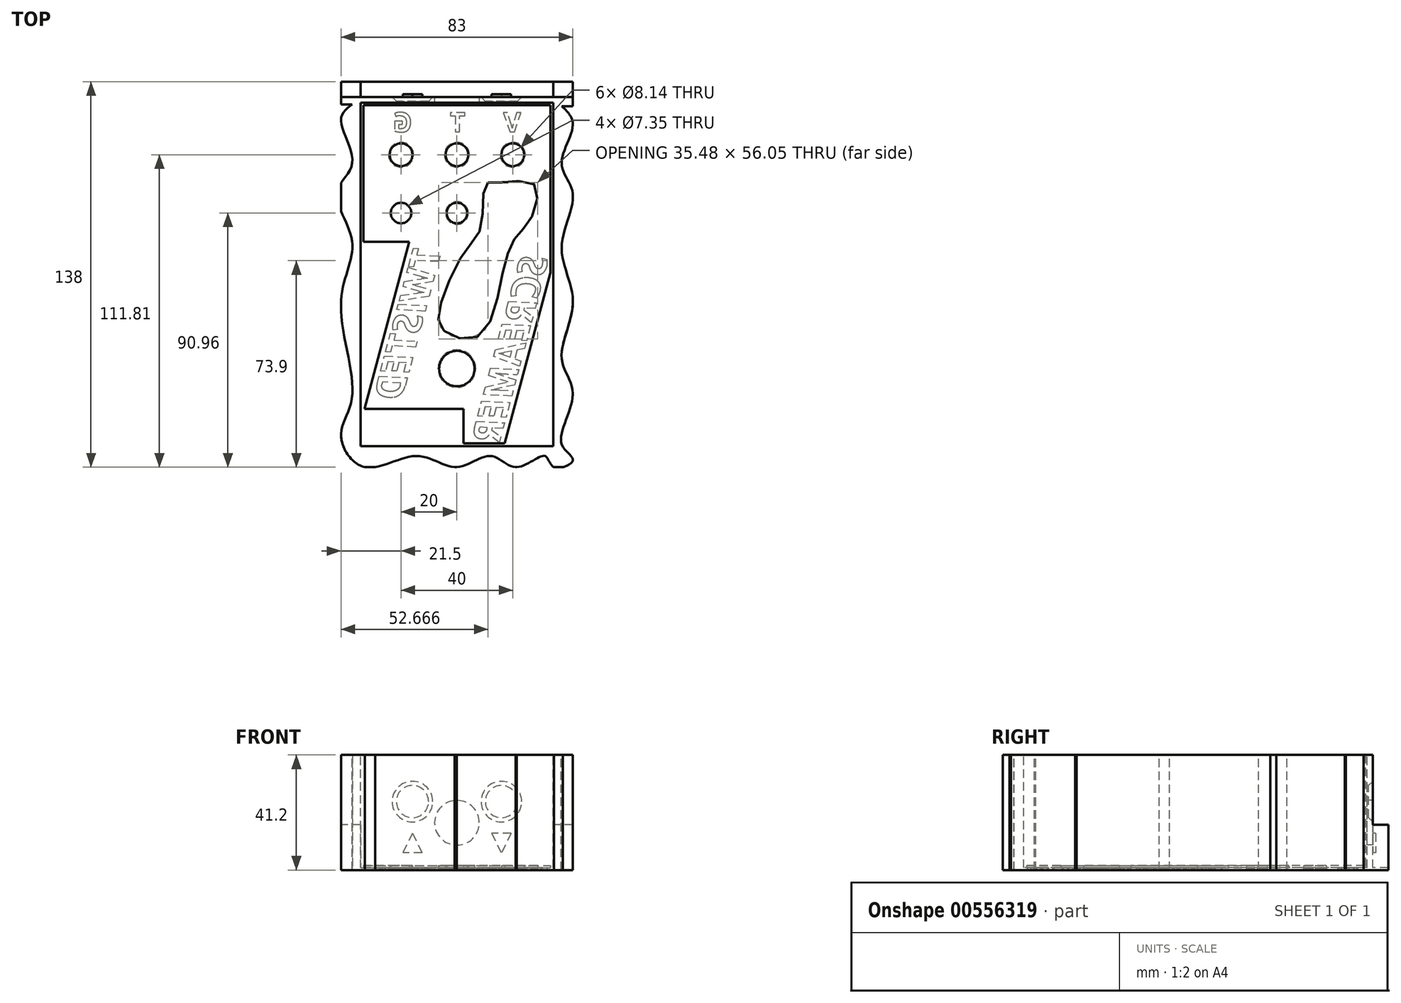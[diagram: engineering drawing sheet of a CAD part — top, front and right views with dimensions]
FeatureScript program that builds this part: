
annotation { "Feature Type Name" : "Feature", "Feature Type Description" : "" }
export const myFeature = defineFeature(function(context is Context, id is Id, definition is map)
    precondition{}
    {
        {
            var Q0;
            Q0=qCreatedBy(makeId("Top.planeOp"),FACE);
            var sketch = newSketch(context, id + "F0", { "sketchPlane" : qUnion([Q0])});
            skLineSegment(sketch, "E0.bottom", {"start": v(-41.5, 69) * mm, "end": v(41.5, 69) * mm});
            skLineSegment(sketch, "E0.top", {"start": v(-41.5, -69) * mm, "end": v(41.5, -69) * mm});
            skLineSegment(sketch, "E0.left", {"start": v(-41.5, 69) * mm, "end": v(-41.5, -69) * mm});
            skLineSegment(sketch, "E0.right", {"start": v(41.5, 69) * mm, "end": v(41.5, -69) * mm});
            skSolve(sketch);
        }
        {
            var Q0;
            Q0=makeQuery(id+"F0.imprint","IMPRINT",FACE,{"disambiguationData":[TD([[makeQuery(id+"F0.imprint","IMPRINT",EDGE,{"derivedFrom":sQuery(id+"F0.wireOp",EDGE,"E0.bottom")}),-1.0]])]});
            extrude(context, id + "F1", {"entities" : qUnion([Q0]), "depth" : 41.2 * mm, "offsetDistance" : 25 * mm});
        }
        {
            var Q0;
            Q0=makeQuery(id+"F1.opExtrude","CAP_FACE",FACE,{"disambiguationData":[OSD([sQuery(id+"F0.wireOp",EDGE,"E0.bottom"),sQuery(id+"F0.wireOp",EDGE,"E0.top"),sQuery(id+"F0.wireOp",EDGE,"E0.left"),sQuery(id+"F0.wireOp",EDGE,"E0.right")])],"isStart":false});
            var sketch = newSketch(context, id + "F2", { "sketchPlane" : qUnion([Q0])});
            skLineSegment(sketch, "E1.bottom", {"start": v(-34.5, 61.5) * mm, "end": v(34.5, 61.5) * mm});
            skLineSegment(sketch, "E1.top", {"start": v(-34.5, -61.5) * mm, "end": v(34.5, -61.5) * mm});
            skLineSegment(sketch, "E1.left", {"start": v(-34.5, 61.5) * mm, "end": v(-34.5, -61.5) * mm});
            skLineSegment(sketch, "E1.right", {"start": v(34.5, 61.5) * mm, "end": v(34.5, -61.5) * mm});
            skSolve(sketch);
        }
        {
            var Q0;
            Q0=makeQuery(id+"F2.imprint","IMPRINT",FACE,{"disambiguationData":[TD([[makeQuery(id+"F2.imprint","IMPRINT",EDGE,{"derivedFrom":sQuery(id+"F2.wireOp",EDGE,"E1.bottom")}),-1.0]])]});
            extrude(context, id + "F3", {"entities" : qUnion([Q0]), "operationType" : NewBodyOperationType.REMOVE, "oppositeDirection" : true, "depth" : 40.4 * mm, "offsetDistance" : 25 * mm});
        }
        {
            var Q0;
            Q0=makeQuery(id+"F3.boolean.opBoolean","COPY",FACE,{"derivedFrom":makeQuery(id+"F3.opExtrude","CAP_FACE",FACE,{"disambiguationData":[OSD([sQuery(id+"F2.wireOp",EDGE,"E1.bottom"),sQuery(id+"F2.wireOp",EDGE,"E1.top"),sQuery(id+"F2.wireOp",EDGE,"E1.left"),sQuery(id+"F2.wireOp",EDGE,"E1.right")])],"isStart":false})});
            var sketch = newSketch(context, id + "F4", { "sketchPlane" : qUnion([Q0])});
            skCircle(sketch, "E2", {"center": v(-20, 42.8) * mm, "radius": 4.07 * mm});
            skCircle(sketch, "E3", {"center": v(0, 42.8) * mm, "radius": 4.07 * mm});
            skCircle(sketch, "E4", {"center": v(20, 42.8) * mm, "radius": 4.07 * mm});
            skCircle(sketch, "E5", {"center": v(0, -33.73) * mm, "radius": 6.35 * mm});
            skLineSegment(sketch, "E6", {"start": v(20, 42.8) * mm, "end": v(0, 42.8) * mm, "construction": true});
            skCircle(sketch, "E7", {"center": v(0, 21.96) * mm, "radius": 3.67 * mm});
            skCircle(sketch, "E8", {"center": v(-20, 21.96) * mm, "radius": 3.67 * mm});
            skSolve(sketch);
        }
        {
            var Q0;
            Q0=qSketchRegion(id+"F4",true);
            extrude(context, id + "F5", {"entities" : qUnion([Q0]), "operationType" : NewBodyOperationType.REMOVE, "oppositeDirection" : true, "depth" : 25 * mm, "offsetDistance" : 25 * mm});
        }
        {
            var Q0;
            Q0=makeQuery(id+"F3.boolean.opBoolean","COPY",FACE,{"derivedFrom":makeQuery(id+"F3.opExtrude","SWEPT_FACE",FACE,{"disambiguationData":[OSD([sQuery(id+"F2.wireOp",EDGE,"E1.bottom")])]})});
            cPlane(context, id + "F6", {"entities" : qUnion([Q0]), "cplaneType" : CPlaneType.OFFSET, "offset" : 2 * mm, "oppositeDirection" : true, "width" : 150 * mm, "height" : 150 * mm});
        }
        {
            var Q0;
            Q0=qCreatedBy(id+"F6.planeOp",FACE);
            var sketch = newSketch(context, id + "F7", { "sketchPlane" : qUnion([Q0])});
            skCircle(sketch, "E9", {"center": v(0, 16.93) * mm, "radius": 8 * mm});
            skCircle(sketch, "E10", {"center": v(15.92, 24.5) * mm, "radius": 5.76 * mm});
            skCircle(sketch, "E11", {"center": v(-15.92, 24.5) * mm, "radius": 5.76 * mm});
            skSolve(sketch);
        }
        {
            var Q0;
            Q0=qSketchRegion(id+"F7",true);
            extrude(context, id + "F8", {"entities" : qUnion([Q0]), "operationType" : NewBodyOperationType.REMOVE, "endBound" : BoundingType.SYMMETRIC, "oppositeDirection" : true, "depth" : 30 * mm, "offsetDistance" : 25 * mm});
        }
        {
            var Q0;
            Q0=qCreatedBy(id+"F6.planeOp",FACE);
            var sketch = newSketch(context, id + "F9", { "sketchPlane" : qUnion([Q0])});
            skLineSegment(sketch, "E12.0", {"start": v(-34.5, 0.8) * mm, "end": v(-34.5, 41.2) * mm});
            skLineSegment(sketch, "E13.0", {"start": v(-34.5, 0.8) * mm, "end": v(34.5, 0.8) * mm});
            skLineSegment(sketch, "E14.0", {"start": v(34.5, 0.8) * mm, "end": v(34.5, 41.2) * mm});
            skLineSegment(sketch, "E15.0", {"start": v(-34.5, 41.2) * mm, "end": v(34.5, 41.2) * mm});
            skSolve(sketch);
        }
        {
            var Q0;
            Q0=qSketchRegion(id+"F9",true);
            extrude(context, id + "F10", {"entities" : qUnion([Q0]), "operationType" : NewBodyOperationType.REMOVE, "oppositeDirection" : true, "depth" : 25 * mm, "offsetDistance" : 25 * mm});
        }
        {
            var Q0;
            Q0=qCreatedBy(makeId("Front.planeOp"),FACE);
            cPlane(context, id + "F11", {"entities" : qUnion([Q0]), "cplaneType" : CPlaneType.OFFSET, "offset" : 38 * mm, "width" : 150 * mm, "height" : 150 * mm});
        }
        {
            var Q0;
            Q0=makeQuery(id+"F1.opExtrude","CAP_FACE",FACE,{"disambiguationData":[OSD([sQuery(id+"F0.wireOp",EDGE,"E0.bottom"),sQuery(id+"F0.wireOp",EDGE,"E0.top"),sQuery(id+"F0.wireOp",EDGE,"E0.left"),sQuery(id+"F0.wireOp",EDGE,"E0.right")])],"isStart":true});
            var sketch = newSketch(context, id + "F12", { "sketchPlane" : qUnion([Q0])});
            skText(sketch, "E16", { "text": "V", "fontName": "OpenSans-Bold.ttf"});
            skText(sketch, "E17", { "text": "T", "fontName": "OpenSans-Bold.ttf"});
            skText(sketch, "E18", { "text": "G", "fontName": "OpenSans-Bold.ttf"});
            const initialGuessF12  = {"E16": [0.02295, -0.051, -1, 0, 0.007], "E17": [0.00303, -0.051, -1, 0, 0.007], "E18": [-0.016, -0.051, -1, 0, 0.007]};
            skSetInitialGuess(sketch, initialGuessF12);
            skSolve(sketch);
        }
        {
            var Q0;
            Q0=qSketchRegion(id+"F12",true);
            extrude(context, id + "F13", {"entities" : qUnion([Q0]), "operationType" : NewBodyOperationType.REMOVE, "endBound" : BoundingType.THROUGH_ALL, "oppositeDirection" : true, "depth" : 0.5 * mm, "offsetDistance" : 25 * mm});
        }
        {
            var Q0;
            Q0=makeQuery(id+"F10.boolean.opBoolean","COPY",FACE,{"derivedFrom":makeQuery(id+"F10.opExtrude","CAP_FACE",FACE,{"disambiguationData":[OSD([sQuery(id+"F9.wireOp",EDGE,"E12.0"),sQuery(id+"F9.wireOp",EDGE,"E13.0"),sQuery(id+"F9.wireOp",EDGE,"E14.0"),sQuery(id+"F9.wireOp",EDGE,"E15.0")])],"isStart":true})});
            var sketch = newSketch(context, id + "F14", { "sketchPlane" : qUnion([Q0])});
            skLineSegment(sketch, "E19", {"start": v(75, 16.26) * mm, "end": v(-75, 16.26) * mm});
            skLineSegment(sketch, "E20", {"start": v(-75, 16.26) * mm, "end": v(-75, 44.5) * mm});
            skLineSegment(sketch, "E21", {"start": v(-75, 44.5) * mm, "end": v(75, 44.5) * mm});
            skLineSegment(sketch, "E22", {"start": v(75, 44.5) * mm, "end": v(75, 16.26) * mm});
            skSolve(sketch);
        }
        {
            var Q0;
            Q0=qSketchRegion(id+"F14",true);
            extrude(context, id + "F15", {"entities" : qUnion([Q0]), "operationType" : NewBodyOperationType.REMOVE, "depth" : 15 * mm, "offsetDistance" : 25 * mm});
        }
        {
            var Q0;
            Q0=makeQuery(id+"F10.boolean.opBoolean","INTERSECT",EDGE,{"derivedFrom":[makeQuery(id+"F8.boolean.opBoolean","COPY",FACE,{"derivedFrom":makeQuery(id+"F8.opExtrude","SWEPT_FACE",FACE,{"disambiguationData":[OSD([sQuery(id+"F7.wireOp",EDGE,"E11")])]})}),makeQuery(id+"F10.opExtrude","CAP_FACE",FACE,{"disambiguationData":[OSD([sQuery(id+"F9.wireOp",EDGE,"E12.0"),sQuery(id+"F9.wireOp",EDGE,"E13.0"),sQuery(id+"F9.wireOp",EDGE,"E14.0"),sQuery(id+"F9.wireOp",EDGE,"E15.0")])],"isStart":true})]});
            var Q1;
            Q1=makeQuery(id+"F10.boolean.opBoolean","INTERSECT",EDGE,{"derivedFrom":[makeQuery(id+"F8.boolean.opBoolean","COPY",FACE,{"derivedFrom":makeQuery(id+"F8.opExtrude","SWEPT_FACE",FACE,{"disambiguationData":[OSD([sQuery(id+"F7.wireOp",EDGE,"E10")])]})}),makeQuery(id+"F10.opExtrude","CAP_FACE",FACE,{"disambiguationData":[OSD([sQuery(id+"F9.wireOp",EDGE,"E12.0"),sQuery(id+"F9.wireOp",EDGE,"E13.0"),sQuery(id+"F9.wireOp",EDGE,"E14.0"),sQuery(id+"F9.wireOp",EDGE,"E15.0")])],"isStart":true})]});
            chamfer(context, id + "F16", {"entities" : qUnion([Q0, Q1]), "width" : 1.5 * mm, "tangentPropagation" : true});
        }
        {
            var Q0;
            {var subQ0=sQuery(id+"F0.wireOp",EDGE,"E0.bottom");var subQ1=sQuery(id+"F0.wireOp",EDGE,"E0.top");var subQ2=sQuery(id+"F0.wireOp",EDGE,"E0.left");var subQ3=sQuery(id+"F0.wireOp",EDGE,"E0.right");Q0=makeQuery(id+"F5.boolean.opBoolean","INTERSECT",EDGE,{"derivedFrom":[makeQuery(id+"FQprxNytQJiPlJy_1.boolean.opBoolean","MERGE",FACE,{"derivedFrom":[makeQuery(id+"F1.opExtrude","CAP_FACE",FACE,{"disambiguationData":[OSD([subQ0,subQ1,subQ2,subQ3])],"isStart":true}),makeQuery(id+"FQprxNytQJiPlJy_1.opLoft","CAP_FACE",FACE,{"disambiguationData":[OSD([makeQuery(id+"Fslz2SRBjreVvUc_1.imprint","IMPRINT",FACE,{"disambiguationData":[TD([[makeQuery(id+"Fslz2SRBjreVvUc_1.imprint","IMPRINT",EDGE,{"derivedFrom":makeQuery(id+"F1.opExtrude","CAP_EDGE",EDGE,{"disambiguationData":[OSD([subQ0])],"isStart":true})}),1.0]])]})])],"isStart":true})]}),makeQuery(id+"F5.opExtrude","SWEPT_FACE",FACE,{"disambiguationData":[OSD([sQuery(id+"F4.wireOp",EDGE,"E4")])]})]});}
            var Q1;
            {var subQ0=sQuery(id+"F0.wireOp",EDGE,"E0.bottom");var subQ1=sQuery(id+"F0.wireOp",EDGE,"E0.top");var subQ2=sQuery(id+"F0.wireOp",EDGE,"E0.left");var subQ3=sQuery(id+"F0.wireOp",EDGE,"E0.right");Q1=makeQuery(id+"F5.boolean.opBoolean","INTERSECT",EDGE,{"derivedFrom":[makeQuery(id+"FQprxNytQJiPlJy_1.boolean.opBoolean","MERGE",FACE,{"derivedFrom":[makeQuery(id+"F1.opExtrude","CAP_FACE",FACE,{"disambiguationData":[OSD([subQ0,subQ1,subQ2,subQ3])],"isStart":true}),makeQuery(id+"FQprxNytQJiPlJy_1.opLoft","CAP_FACE",FACE,{"disambiguationData":[OSD([makeQuery(id+"Fslz2SRBjreVvUc_1.imprint","IMPRINT",FACE,{"disambiguationData":[TD([[makeQuery(id+"Fslz2SRBjreVvUc_1.imprint","IMPRINT",EDGE,{"derivedFrom":makeQuery(id+"F1.opExtrude","CAP_EDGE",EDGE,{"disambiguationData":[OSD([subQ0])],"isStart":true})}),1.0]])]})])],"isStart":true})]}),makeQuery(id+"F5.opExtrude","SWEPT_FACE",FACE,{"disambiguationData":[OSD([sQuery(id+"F4.wireOp",EDGE,"E3")])]})]});}
            var Q2;
            {var subQ0=sQuery(id+"F0.wireOp",EDGE,"E0.bottom");var subQ1=sQuery(id+"F0.wireOp",EDGE,"E0.top");var subQ2=sQuery(id+"F0.wireOp",EDGE,"E0.left");var subQ3=sQuery(id+"F0.wireOp",EDGE,"E0.right");Q2=makeQuery(id+"F5.boolean.opBoolean","INTERSECT",EDGE,{"derivedFrom":[makeQuery(id+"FQprxNytQJiPlJy_1.boolean.opBoolean","MERGE",FACE,{"derivedFrom":[makeQuery(id+"F1.opExtrude","CAP_FACE",FACE,{"disambiguationData":[OSD([subQ0,subQ1,subQ2,subQ3])],"isStart":true}),makeQuery(id+"FQprxNytQJiPlJy_1.opLoft","CAP_FACE",FACE,{"disambiguationData":[OSD([makeQuery(id+"Fslz2SRBjreVvUc_1.imprint","IMPRINT",FACE,{"disambiguationData":[TD([[makeQuery(id+"Fslz2SRBjreVvUc_1.imprint","IMPRINT",EDGE,{"derivedFrom":makeQuery(id+"F1.opExtrude","CAP_EDGE",EDGE,{"disambiguationData":[OSD([subQ0])],"isStart":true})}),1.0]])]})])],"isStart":true})]}),makeQuery(id+"F5.opExtrude","SWEPT_FACE",FACE,{"disambiguationData":[OSD([sQuery(id+"F4.wireOp",EDGE,"E2")])]})]});}
            var Q3;
            {var subQ0=sQuery(id+"F0.wireOp",EDGE,"E0.bottom");var subQ1=sQuery(id+"F0.wireOp",EDGE,"E0.top");var subQ2=sQuery(id+"F0.wireOp",EDGE,"E0.left");var subQ3=sQuery(id+"F0.wireOp",EDGE,"E0.right");Q3=makeQuery(id+"F5.boolean.opBoolean","INTERSECT",EDGE,{"derivedFrom":[makeQuery(id+"FQprxNytQJiPlJy_1.boolean.opBoolean","MERGE",FACE,{"derivedFrom":[makeQuery(id+"F1.opExtrude","CAP_FACE",FACE,{"disambiguationData":[OSD([subQ0,subQ1,subQ2,subQ3])],"isStart":true}),makeQuery(id+"FQprxNytQJiPlJy_1.opLoft","CAP_FACE",FACE,{"disambiguationData":[OSD([makeQuery(id+"Fslz2SRBjreVvUc_1.imprint","IMPRINT",FACE,{"disambiguationData":[TD([[makeQuery(id+"Fslz2SRBjreVvUc_1.imprint","IMPRINT",EDGE,{"derivedFrom":makeQuery(id+"F1.opExtrude","CAP_EDGE",EDGE,{"disambiguationData":[OSD([subQ0])],"isStart":true})}),1.0]])]})])],"isStart":true})]}),makeQuery(id+"F5.opExtrude","SWEPT_FACE",FACE,{"disambiguationData":[OSD([sQuery(id+"F4.wireOp",EDGE,"E7")])]})]});}
            var Q4;
            {var subQ0=sQuery(id+"F0.wireOp",EDGE,"E0.bottom");var subQ1=sQuery(id+"F0.wireOp",EDGE,"E0.top");var subQ2=sQuery(id+"F0.wireOp",EDGE,"E0.left");var subQ3=sQuery(id+"F0.wireOp",EDGE,"E0.right");Q4=makeQuery(id+"F5.boolean.opBoolean","INTERSECT",EDGE,{"derivedFrom":[makeQuery(id+"FQprxNytQJiPlJy_1.boolean.opBoolean","MERGE",FACE,{"derivedFrom":[makeQuery(id+"F1.opExtrude","CAP_FACE",FACE,{"disambiguationData":[OSD([subQ0,subQ1,subQ2,subQ3])],"isStart":true}),makeQuery(id+"FQprxNytQJiPlJy_1.opLoft","CAP_FACE",FACE,{"disambiguationData":[OSD([makeQuery(id+"Fslz2SRBjreVvUc_1.imprint","IMPRINT",FACE,{"disambiguationData":[TD([[makeQuery(id+"Fslz2SRBjreVvUc_1.imprint","IMPRINT",EDGE,{"derivedFrom":makeQuery(id+"F1.opExtrude","CAP_EDGE",EDGE,{"disambiguationData":[OSD([subQ0])],"isStart":true})}),1.0]])]})])],"isStart":true})]}),makeQuery(id+"F5.opExtrude","SWEPT_FACE",FACE,{"disambiguationData":[OSD([sQuery(id+"F4.wireOp",EDGE,"KNiFqmuv-MMCi-B5FO-T3GH-z67XstVQp584")])]})]});}
            var Q5;
            {var subQ0=sQuery(id+"F0.wireOp",EDGE,"E0.bottom");var subQ1=sQuery(id+"F0.wireOp",EDGE,"E0.top");var subQ2=sQuery(id+"F0.wireOp",EDGE,"E0.left");var subQ3=sQuery(id+"F0.wireOp",EDGE,"E0.right");Q5=makeQuery(id+"F5.boolean.opBoolean","INTERSECT",EDGE,{"derivedFrom":[makeQuery(id+"FQprxNytQJiPlJy_1.boolean.opBoolean","MERGE",FACE,{"derivedFrom":[makeQuery(id+"F1.opExtrude","CAP_FACE",FACE,{"disambiguationData":[OSD([subQ0,subQ1,subQ2,subQ3])],"isStart":true}),makeQuery(id+"FQprxNytQJiPlJy_1.opLoft","CAP_FACE",FACE,{"disambiguationData":[OSD([makeQuery(id+"Fslz2SRBjreVvUc_1.imprint","IMPRINT",FACE,{"disambiguationData":[TD([[makeQuery(id+"Fslz2SRBjreVvUc_1.imprint","IMPRINT",EDGE,{"derivedFrom":makeQuery(id+"F1.opExtrude","CAP_EDGE",EDGE,{"disambiguationData":[OSD([subQ0])],"isStart":true})}),1.0]])]})])],"isStart":true})]}),makeQuery(id+"F5.opExtrude","SWEPT_FACE",FACE,{"disambiguationData":[OSD([sQuery(id+"F4.wireOp",EDGE,"E5")])]})]});}
            chamfer(context, id + "F17", {"entities" : qUnion([Q0, Q1, Q2, Q3, Q4, Q5]), "width" : 0.4 * mm, "tangentPropagation" : true});
        }
        {
            var Q0;
            {var subQ0=sQuery(id+"F0.wireOp",EDGE,"E0.bottom");var subQ1=sQuery(id+"F0.wireOp",EDGE,"E0.top");var subQ2=sQuery(id+"F0.wireOp",EDGE,"E0.left");var subQ3=sQuery(id+"F0.wireOp",EDGE,"E0.right");Q0=makeQuery(id+"FQprxNytQJiPlJy_1.boolean.opBoolean","MERGE",FACE,{"derivedFrom":[makeQuery(id+"F1.opExtrude","CAP_FACE",FACE,{"disambiguationData":[OSD([subQ0,subQ1,subQ2,subQ3])],"isStart":true}),makeQuery(id+"FQprxNytQJiPlJy_1.opLoft","CAP_FACE",FACE,{"disambiguationData":[OSD([makeQuery(id+"Fslz2SRBjreVvUc_1.imprint","IMPRINT",FACE,{"disambiguationData":[TD([[makeQuery(id+"Fslz2SRBjreVvUc_1.imprint","IMPRINT",EDGE,{"derivedFrom":makeQuery(id+"F1.opExtrude","CAP_EDGE",EDGE,{"disambiguationData":[OSD([subQ0])],"isStart":true})}),1.0]])]})])],"isStart":true})]});}
            var sketch = newSketch(context, id + "F18", { "sketchPlane" : qUnion([Q0])});
            skText(sketch, "E23", { "text": "  TWISTED\n\nSCREAMER", "fontName": "OpenSans-BoldItalic.ttf"});
            const initialGuessF18  = {"E23": [-0.00375, -0.01526, -0.25882, 0.96593, 0.01]};
            skSetInitialGuess(sketch, initialGuessF18);
            skSolve(sketch);
        }
        {
            var Q0;
            Q0=qSketchRegion(id+"F18",true);
            extrude(context, id + "F19", {"entities" : qUnion([Q0]), "operationType" : NewBodyOperationType.REMOVE, "endBound" : BoundingType.THROUGH_ALL, "oppositeDirection" : true, "depth" : 25 * mm, "offsetDistance" : 25 * mm, "hasSecondDirection" : true, "secondDirectionBound" : SecondDirectionBoundingType.THROUGH_ALL, "secondDirectionOppositeDirection" : false, "secondDirectionDepth" : 25 * mm});
        }
        {
            var Q0;
            Q0=makeQuery(id+"F15.boolean.opBoolean","MERGE",FACE,{"derivedFrom":[makeQuery(id+"F10.boolean.opBoolean","COPY",FACE,{"derivedFrom":makeQuery(id+"F10.opExtrude","CAP_FACE",FACE,{"disambiguationData":[OSD([sQuery(id+"F9.wireOp",EDGE,"E12.0"),sQuery(id+"F9.wireOp",EDGE,"E13.0"),sQuery(id+"F9.wireOp",EDGE,"E14.0"),sQuery(id+"F9.wireOp",EDGE,"E15.0")])],"isStart":true})}),makeQuery(id+"F15.opExtrude","CAP_FACE",FACE,{"disambiguationData":[OSD([sQuery(id+"F14.wireOp",EDGE,"E19"),sQuery(id+"F14.wireOp",EDGE,"E20"),sQuery(id+"F14.wireOp",EDGE,"E21"),sQuery(id+"F14.wireOp",EDGE,"E22")])],"isStart":true})]});
            var sketch = newSketch(context, id + "F20", { "sketchPlane" : qUnion([Q0])});
            skLineSegment(sketch, "E24", {"start": v(15.92, 24.5) * mm, "end": v(15.92, 6.07) * mm, "construction": true});
            skLineSegment(sketch, "E25", {"start": v(-15.92, 24.5) * mm, "end": v(-15.92, 6.07) * mm, "construction": true});
            skLineSegment(sketch, "E26", {"start": v(-19.42, 13.12) * mm, "end": v(-15.92, 13.12) * mm});
            skLineSegment(sketch, "E27", {"start": v(-19.42, 13.12) * mm, "end": v(-15.92, 6.12) * mm});
            skLineSegment(sketch, "E28", {"start": v(15.92, 13.12) * mm, "end": v(19.42, 6.12) * mm});
            skLineSegment(sketch, "E29", {"start": v(19.42, 6.12) * mm, "end": v(15.92, 6.12) * mm});
            skLineSegment(sketch, "E30.MirrorCS", {"start": v(12.42, 6.12) * mm, "end": v(15.92, 6.12) * mm});
            skLineSegment(sketch, "E31.MirrorCS", {"start": v(15.92, 13.12) * mm, "end": v(12.42, 6.12) * mm});
            skLineSegment(sketch, "E32.MirrorCS", {"start": v(-12.42, 13.12) * mm, "end": v(-15.92, 6.12) * mm});
            skLineSegment(sketch, "E33.MirrorCS", {"start": v(-12.42, 13.12) * mm, "end": v(-15.92, 13.12) * mm});
            skSolve(sketch);
        }
        {
            var Q0;
            Q0=qSketchRegion(id+"F20",true);
            extrude(context, id + "F21", {"entities" : qUnion([Q0]), "operationType" : NewBodyOperationType.ADD, "depth" : 1 * mm, "offsetDistance" : 25 * mm});
        }
        {
            var Q0;
            {var subQ0=sQuery(id+"F2.wireOp",EDGE,"E1.bottom");var subQ1=sQuery(id+"F2.wireOp",EDGE,"E1.left");var subQ2=sQuery(id+"F2.wireOp",EDGE,"E1.top");var subQ3=sQuery(id+"F2.wireOp",EDGE,"E1.right");Q0=makeQuery(id+"F19.boolean.opBoolean","SPLIT",FACE,{"disambiguationData":[TD([makeQuery(id+"F3.boolean.opBoolean","COPY",FACE,{"derivedFrom":makeQuery(id+"F3.opExtrude","SWEPT_FACE",FACE,{"disambiguationData":[OSD([subQ0])]})})])],"derivedFrom":makeQuery(id+"F3.boolean.opBoolean","COPY",FACE,{"derivedFrom":makeQuery(id+"F3.opExtrude","CAP_FACE",FACE,{"disambiguationData":[OSD([subQ0,subQ2,subQ1,subQ3])],"isStart":false})})});}
            var sketch = newSketch(context, id + "F22", { "sketchPlane" : qUnion([Q0])});
            skLineSegment(sketch, "E34.bottom", {"start": v(-33.5, 60.5) * mm, "end": v(33.5, 60.5) * mm});
            skLineSegment(sketch, "E34.top", {"start": v(2.3, -60.5) * mm, "end": v(17.13, -60.5) * mm});
            skLineSegment(sketch, "E34.left", {"start": v(-33.5, 60.5) * mm, "end": v(-33.5, 11.66) * mm});
            skLineSegment(sketch, "E34.right", {"start": v(33.5, 60.5) * mm, "end": v(33.5, 0.6) * mm});
            skPoint(sketch, "E34.middle", {"position": v(0, 0) * mm});
            skCircle(sketch, "E35.0", {"center": v(-20, 42.8) * mm, "radius": 4.07 * mm});
            skCircle(sketch, "E36.0", {"center": v(0, 42.8) * mm, "radius": 4.07 * mm});
            skCircle(sketch, "E37.0", {"center": v(20, 42.8) * mm, "radius": 4.07 * mm});
            skCircle(sketch, "E38.0", {"center": v(0, 21.96) * mm, "radius": 3.67 * mm});
            skCircle(sketch, "E39.0", {"center": v(-20, 21.96) * mm, "radius": 3.68 * mm});
            skCircle(sketch, "E40.0", {"center": v(0, -33.73) * mm, "radius": 6.35 * mm});
            skFitSpline(sketch, "E41", {"points": [v(15.6, 32.92) * mm, v(10.24, 32.07) * mm, v(8.74, 17.26) * mm, v(3.16, 8.67) * mm, v(-6.28, -12.57) * mm, v(-4.57, -20.3) * mm, v(7.88, -22.02) * mm, v(16.25, 0) * mm, v(20.97, 13.18) * mm, v(26.55, 20.26) * mm, v(27.84, 32.07) * mm, v(15.6, 32.92) * mm]});
            skLineSegment(sketch, "E42", {"start": v(-33.1, -48.2) * mm, "end": v(-17.05, 11.66) * mm});
            skLineSegment(sketch, "E43", {"start": v(-17.05, 11.66) * mm, "end": v(-33.5, 11.66) * mm});
            skLineSegment(sketch, "E44", {"start": v(-33.1, -48.2) * mm, "end": v(2.3, -48.2) * mm});
            skLineSegment(sketch, "E45", {"start": v(2.3, -48.2) * mm, "end": v(2.3, -60.5) * mm});
            skPoint(sketch, "E46.orphan", {"position": v(-33.5, -60.5) * mm});
            skLineSegment(sketch, "E47", {"start": v(17.13, -60.5) * mm, "end": v(33.5, 0.6) * mm});
            skPoint(sketch, "E48.orphan", {"position": v(33.5, -60.5) * mm});
            skSolve(sketch);
        }
        {
            var Q0;
            Q0=qSketchRegion(id+"F22",true);
            extrude(context, id + "F23", {"entities" : qUnion([Q0]), "depth" : 0.8 * mm, "offsetDistance" : 25 * mm});
        }
        {
            var Q0;
            Q0=makeQuery(id+"F1.opExtrude","CAP_FACE",FACE,{"disambiguationData":[OSD([sQuery(id+"F0.wireOp",EDGE,"E0.bottom"),sQuery(id+"F0.wireOp",EDGE,"E0.top"),sQuery(id+"F0.wireOp",EDGE,"E0.left"),sQuery(id+"F0.wireOp",EDGE,"E0.right")])],"isStart":false});
            var sketch = newSketch(context, id + "F24", { "sketchPlane" : qUnion([Q0])});
            skLineSegment(sketch, "E49.bottom", {"start": v(37.5, -65) * mm, "end": v(-37.5, -65) * mm, "construction": true});
            skLineSegment(sketch, "E49.left", {"start": v(37.5, -65) * mm, "end": v(37.5, 65) * mm, "construction": true});
            skLineSegment(sketch, "E49.right", {"start": v(-37.5, -65) * mm, "end": v(-37.5, 65) * mm, "construction": true});
            skPoint(sketch, "E49.middle", {"position": v(0, 0) * mm});
            skFitSpline(sketch, "E50", {"points": [v(37.5, 60.21) * mm, v(41.5, 53.5) * mm, v(37.5, 39.72) * mm, v(41.5, 28.87) * mm, v(37.5, 9.73) * mm, v(41.5, -9.78) * mm, v(37.5, -30.22) * mm, v(41.5, -43.1) * mm, v(37.5, -60.8) * mm, v(41.5, -66.53) * mm, v(34.79, -69) * mm, v(31.45, -65) * mm, v(21.43, -69) * mm, v(12.18, -65) * mm, v(0, -69) * mm, v(-14.25, -65) * mm, v(-32.93, -69) * mm, v(-41.5, -57.63) * mm, v(-37.5, -43.68) * mm, v(-41.5, -9.35) * mm, v(-37.5, 11.9) * mm, v(-43.02, 29.28) * mm, v(-37.5, 39.8) * mm, v(-41.5, 55.25) * mm, v(-37.5, 60.83) * mm], "startDerivative": vector(196.39, -185.6) * mm, "endDerivative": vector(205.12, 151.33) * mm});
            skLineSegment(sketch, "E51", {"start": v(37.5, 60.21) * mm, "end": v(46.67, 60.21) * mm});
            skLineSegment(sketch, "E52", {"start": v(46.67, 60.21) * mm, "end": v(46.67, -78.28) * mm});
            skLineSegment(sketch, "E53", {"start": v(46.67, -78.28) * mm, "end": v(-48.04, -78.28) * mm});
            skLineSegment(sketch, "E54", {"start": v(-48.04, -78.28) * mm, "end": v(-48.04, 60.83) * mm});
            skLineSegment(sketch, "E55", {"start": v(-48.04, 60.83) * mm, "end": v(-37.5, 60.83) * mm});
            skSolve(sketch);
        }
        {
            var Q0;
            Q0 = qSketchRegion(id + "F24", true);
            extrude(context, id + "F25", {"entities" : qUnion([Q0]), "operationType" : NewBodyOperationType.REMOVE, "oppositeDirection" : true, "depth" : 46.7 * mm, "offsetDistance" : 25 * mm});
        }
    });
